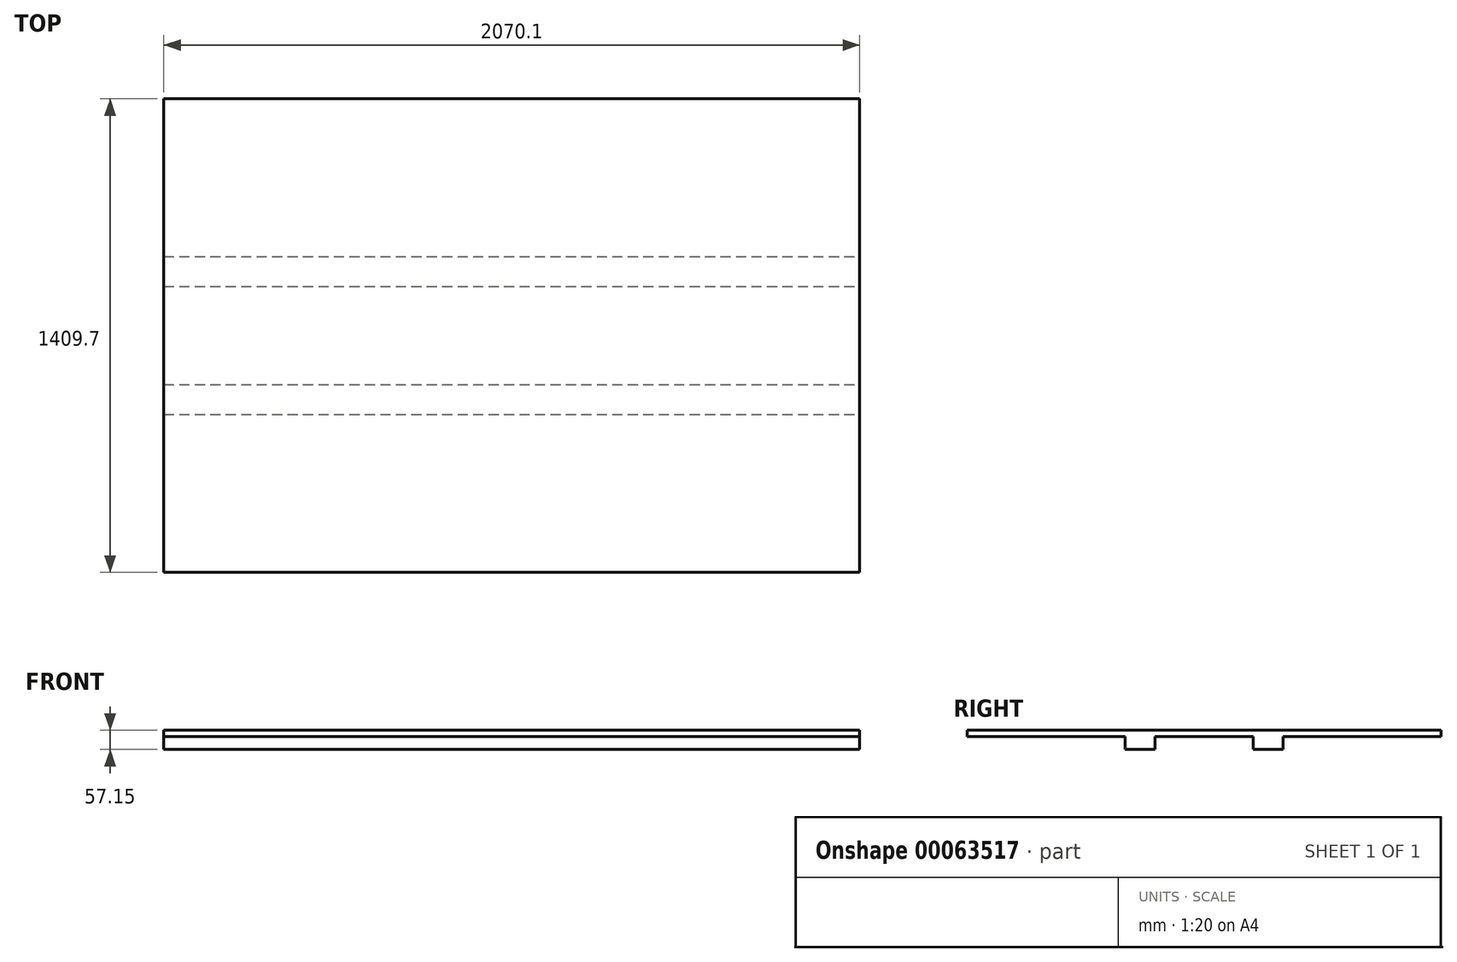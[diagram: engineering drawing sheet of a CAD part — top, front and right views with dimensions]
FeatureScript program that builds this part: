
annotation { "Feature Type Name" : "Feature", "Feature Type Description" : "" }
export const myFeature = defineFeature(function(context is Context, id is Id, definition is map)
    precondition{}
    {
        {
            var Q0;
            Q0=qCreatedBy(makeId("Top.planeOp"),FACE);
            var sketch = newSketch(context, id + "F0", { "sketchPlane" : qUnion([Q0])});
            skLineSegment(sketch, "E0.rect.bottom", {"start": v(-1035.05, 704.85) * mm, "end": v(1035.05, 704.85) * mm});
            skLineSegment(sketch, "E0.rect.top", {"start": v(-1035.05, -704.85) * mm, "end": v(1035.05, -704.85) * mm});
            skLineSegment(sketch, "E0.rect.left", {"start": v(-1035.05, 704.85) * mm, "end": v(-1035.05, -704.85) * mm});
            skLineSegment(sketch, "E0.rect.right", {"start": v(1035.05, 704.85) * mm, "end": v(1035.05, -704.85) * mm});
            skPoint(sketch, "E0.rect.middle", {"position": v(0, 0) * mm});
            skSolve(sketch);
        }
        {
            var Q0;
            Q0=makeQuery(id+"F0.imprint","IMPRINT",FACE,{"disambiguationData":[TD([[makeQuery(id+"F0.imprint","IMPRINT",EDGE,{"derivedFrom":sQuery(id+"F0.wireOp",EDGE,"E0.rect.bottom")}),-1.0]])]});
            extrude(context, id + "F1", {"entities" : qUnion([Q0]), "depth" : 19.05 * mm});
        }
        {
            var Q0;
            Q0=makeQuery(id+"F1.opExtrude","CAP_FACE",FACE,{"disambiguationData":[OSD([sQuery(id+"F0.wireOp",EDGE,"E0.rect.bottom"),sQuery(id+"F0.wireOp",EDGE,"E0.rect.top"),sQuery(id+"F0.wireOp",EDGE,"E0.rect.left"),sQuery(id+"F0.wireOp",EDGE,"E0.rect.right")])],"isStart":true});
            var sketch = newSketch(context, id + "F2", { "sketchPlane" : qUnion([Q0])});
            skLineSegment(sketch, "E1.bottom", {"start": v(-1035.05, 234.95) * mm, "end": v(1035.05, 234.95) * mm});
            skLineSegment(sketch, "E1.top", {"start": v(-1035.05, 146.05) * mm, "end": v(1035.05, 146.05) * mm});
            skLineSegment(sketch, "E1.left", {"start": v(-1035.05, 234.95) * mm, "end": v(-1035.05, 146.05) * mm});
            skLineSegment(sketch, "E1.right", {"start": v(1035.05, 234.95) * mm, "end": v(1035.05, 146.05) * mm});
            skLineSegment(sketch, "E2.bottom", {"start": v(-1035.05, -146.05) * mm, "end": v(1035.05, -146.05) * mm});
            skLineSegment(sketch, "E2.top", {"start": v(-1035.05, -234.95) * mm, "end": v(1035.05, -234.95) * mm});
            skLineSegment(sketch, "E2.left", {"start": v(-1035.05, -146.05) * mm, "end": v(-1035.05, -234.95) * mm});
            skLineSegment(sketch, "E2.right", {"start": v(1035.05, -146.05) * mm, "end": v(1035.05, -234.95) * mm});
            skSolve(sketch);
        }
        {
            var Q0;
            Q0=makeQuery(id+"F2.imprint","IMPRINT",FACE,{"disambiguationData":[TD([[makeQuery(id+"F2.imprint","IMPRINT",EDGE,{"derivedFrom":sQuery(id+"F2.wireOp",EDGE,"E1.bottom")}),-1.0]])]});
            var Q1;
            Q1=makeQuery(id+"F2.imprint","IMPRINT",FACE,{"disambiguationData":[TD([[makeQuery(id+"F2.imprint","IMPRINT",EDGE,{"derivedFrom":sQuery(id+"F2.wireOp",EDGE,"E2.bottom")}),-1.0]])]});
            extrude(context, id + "F3", {"entities" : qUnion([Q0, Q1]), "operationType" : NewBodyOperationType.ADD, "depth" : 38.1 * mm});
        }
    });
